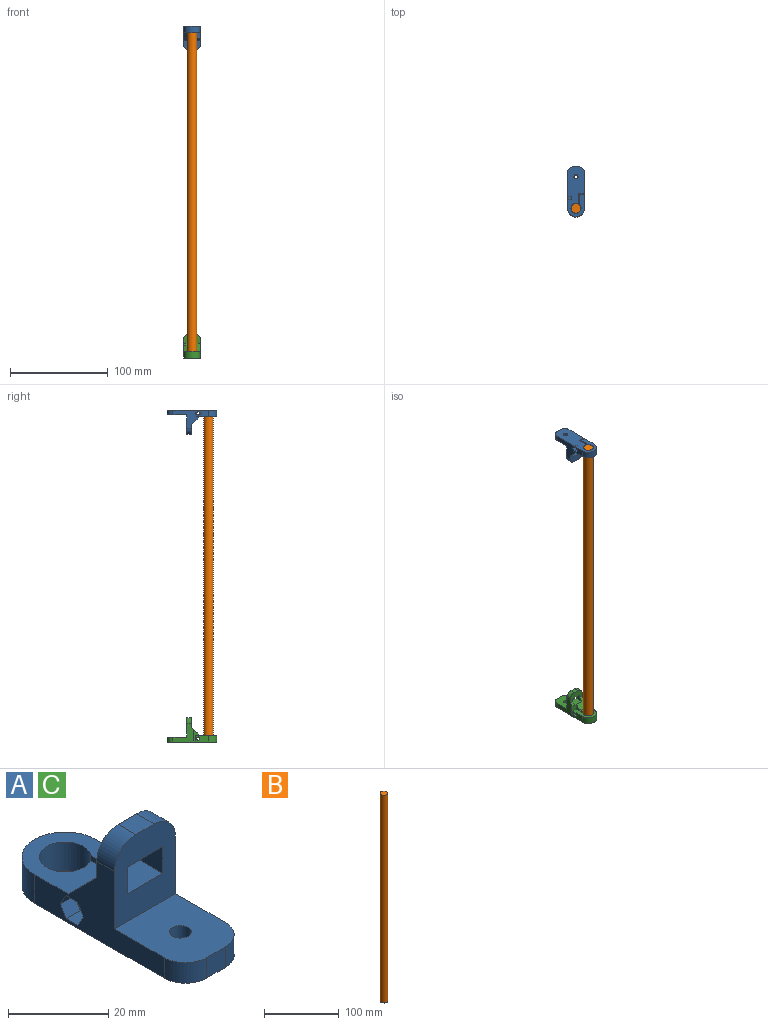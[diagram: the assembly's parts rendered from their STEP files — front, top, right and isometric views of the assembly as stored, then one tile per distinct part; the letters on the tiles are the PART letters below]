
ASSEMBLY  parts=3 mates=2
PART A: 36 faces, bbox 17.2x51.1x25 mm
  f0: plane 11.23x8mm, normal (0,0.71,0.71), area 92mm2, adj f2,f6,f14,f18,f27,f30
  f1: plane 20x17.2mm, normal (0,-1,0), area 263.5mm2, adj f4,f13,f14,f17,f27,f28,f29,f30
  f2: plane 17.2x10mm, normal (0,1,0), area 124mm2, adj f0,f4,f13,f14,f28,f29,f30,f33
  f3: cylinder r=1.65mm len=7.23mm, axis (-1,0,0), area 75mm2, adj f6,f26
  f4: plane 21.5x19mm, normal (1,0,0), area 199.4mm2, adj f1,f2,f5,f16,f17,f32,f34,f35
  f5: plane 12.5x5.97mm, normal (0,1,0), area 72.8mm2, adj f4,f6,f16,f27,f28,f35
  f6: plane 11.75x10.57mm, normal (1,0,0), area 80.3mm2, adj f0,f3,f5,f7,f16,f18,f27
  f7: cylinder r=5.15mm len=10.3mm, axis (0,0,-1), area 213.4mm2, adj f6,f8,f16,f18
  f8: plane 10.4x7mm, normal (-1,0,0), area 64.2mm2, adj f7,f9,f16,f18,f19
  f9: plane 7x4.57mm, normal (0,-1,0), area 32mm2, adj f8,f10,f16,f18
  f10: plane 13.6x7mm, normal (1,0,0), area 86.6mm2, adj f9,f11,f16,f18,f19
  f11: cylinder r=8.6mm len=17.2mm, axis (0,0,-1), area 189.1mm2, adj f10,f14,f16,f18
  f12: cylinder r=2.15mm len=5mm, axis (0,0,-1), area 67.5mm2, adj f16,f17
  f13: plane 5.2x5mm, normal (0,0,1), area 26mm2, adj f1,f2,f33,f34
  f14: plane 36.5x19mm, normal (-1,0,0), area 292.3mm2, adj f0,f1,f2,f11,f16,f17,f18,f20
  f15: plane 5.2x5mm, normal (0,-1,0), area 26mm2, adj f16,f17,f31,f32
  f16: plane 51.1x17.2mm, normal (0,0,-1), area 711.9mm2, adj f4,f5,f6,f7,f8,f9,f10,f11
  f17: plane 20x17.2mm, normal (0,0,1), area 314mm2, adj f1,f4,f12,f14,f15,f31,f32
  f18: plane 22.2x17.2mm, normal (0,0,1), area 207.1mm2, adj f0,f6,f7,f8,f9,f10,f11,f14
  f19: cylinder r=1.65mm len=4.57mm, axis (-1,0,0), area 47.3mm2, adj f8,f10
  f20: plane 4x3.23mm, normal (0,0,-1), area 12.9mm2, adj f14,f21,f25,f26
  f21: plane 4x2.8mm, normal (0,-0.87,-0.5), area 12.9mm2, adj f14,f20,f22,f26
  f22: plane 4x2.8mm, normal (0,-0.87,0.5), area 12.9mm2, adj f14,f21,f23,f26
  f23: plane 4x3.23mm, normal (0,0,1), area 12.9mm2, adj f14,f22,f24,f26
  f24: plane 4x2.8mm, normal (0,0.87,0.5), area 12.9mm2, adj f14,f23,f25,f26
  f25: plane 4x2.8mm, normal (0,0.87,-0.5), area 12.9mm2, adj f14,f20,f24,f26
  f26: plane 6.47x5.6mm, normal (-1,0,0), area 18.6mm2, adj f3,f20,f21,f22,f23,f24,f25
  f27: plane 10x8.25mm, normal (0,0,1), area 80.7mm2, adj f0,f1,f5,f6,f28,f30
  f28: plane 7.5x6.5mm, normal (-1,0,0), area 37.5mm2, adj f1,f2,f5,f27,f29,f35
  f29: plane 10x5mm, normal (0,0,-1), area 50mm2, adj f1,f2,f28,f30
  f30: plane 8.25x6.5mm, normal (1,0,0), area 37.8mm2, adj f0,f1,f2,f27,f29
  f31: cylinder r=6mm len=6mm, axis (0,0,-1), area 47.1mm2, adj f14,f15,f16,f17
  f32: cylinder r=6mm len=6mm, axis (0,0,-1), area 47.1mm2, adj f4,f15,f16,f17
  f33: cylinder r=6mm len=6mm, axis (0,1,0), area 47.1mm2, adj f1,f2,f13,f14
  f34: cylinder r=6mm len=6mm, axis (0,-1,0), area 47.1mm2, adj f1,f2,f4,f13
  f35: plane 3.6x2.5mm, normal (0,0.71,0.71), area 12.7mm2, adj f2,f4,f5,f28
PART B: 3 faces, bbox 10x10x340 mm
  f0: cylinder r=5mm len=340mm, axis (0,0,-1), area 10681.4mm2, adj f1,f2
  f1: plane 10x10mm, normal (0,0,1), area 78.5mm2, adj f0
  f2: plane 10x10mm, normal (0,0,-1), area 78.5mm2, adj f0
PART C: same geometry as A
PLACE A rot(axis=(1,0,0),180deg) t=(-146.83,-1.7,471.92)mm
PLACE B rot(axis=(0,0,-1),180deg) t=(-178.84,-1.7,131.92)mm
PLACE C rot(axis=(0,0,-1),180deg) t=(-146.83,-1.7,131.92)mm
MATE fastened A.f7 <-> B.f0  axis (0,0,1) through (-146.83,-1.7,471.92)mm
MATE fastened C.f7 <-> B.f0  axis (0,0,-1) through (-146.83,-1.7,131.92)mm
